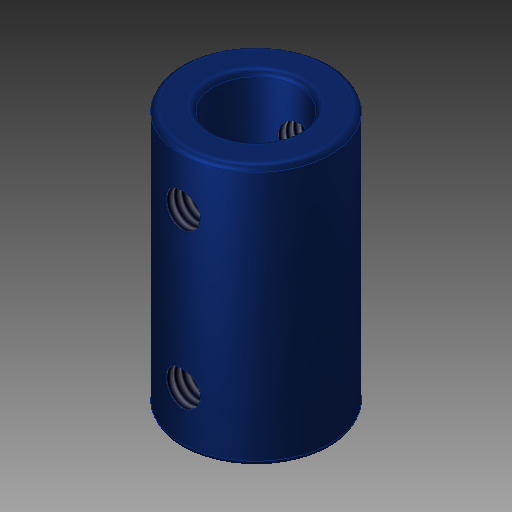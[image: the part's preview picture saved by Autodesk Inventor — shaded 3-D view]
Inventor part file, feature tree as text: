
AUTODESK INVENTOR PART (.ipt)
format: ipt  version: 2019 (Build 230136000, 136)  size: 210,432 bytes
history: native  units: mm
features: sketch x4, extrude x3, fillet x1, plane x1, hole x1
ambient origin geometry x8: Origin, YZ Plane, XZ Plane, XY Plane, X Axis, Y Axis, Z Axis, Center Point
bodies: Solid1 (feature_tree)
feature tree (10):
  extrude  "Extrusion1"  Depth=24.5mm TaperAngle=0.0deg
  extrude  "Extrusion2"  Depth=12.25mm TaperAngle=0.0deg
  extrude  "Extrusion3"  Depth=12.25mm TaperAngle=0.0deg
  fillet  "Fillet1"  Radius=0.5mm
  plane  "Work Plane4"
  hole  "Hole3"  [1 undecoded]
  sketch  "Sketch1"  dims[d0=14.0mm d1=24.5mm d2=0.0mm]
  sketch  "Sketch2"  dims[d3=8.0mm d4=12.25mm d5=0.0mm]
  sketch  "Sketch3"  dims[d6=5.0mm d7=12.25mm d8=0.0mm d9=0.5mm]
  sketch  "Sketch8"  dims[d33=3.0mm d34=5.0mm d38=5.0mm d39=3.242mm d40=8.0mm d41=4.0mm d42=2.0mm d43=90.0deg d44=11.8mm d45=20.594885mm]
note: 1 required parameter value undecoded (feature->parameter linkage not recoverable at this tier; creation-order binding heuristic only, values carry confidence <= 0.55)
